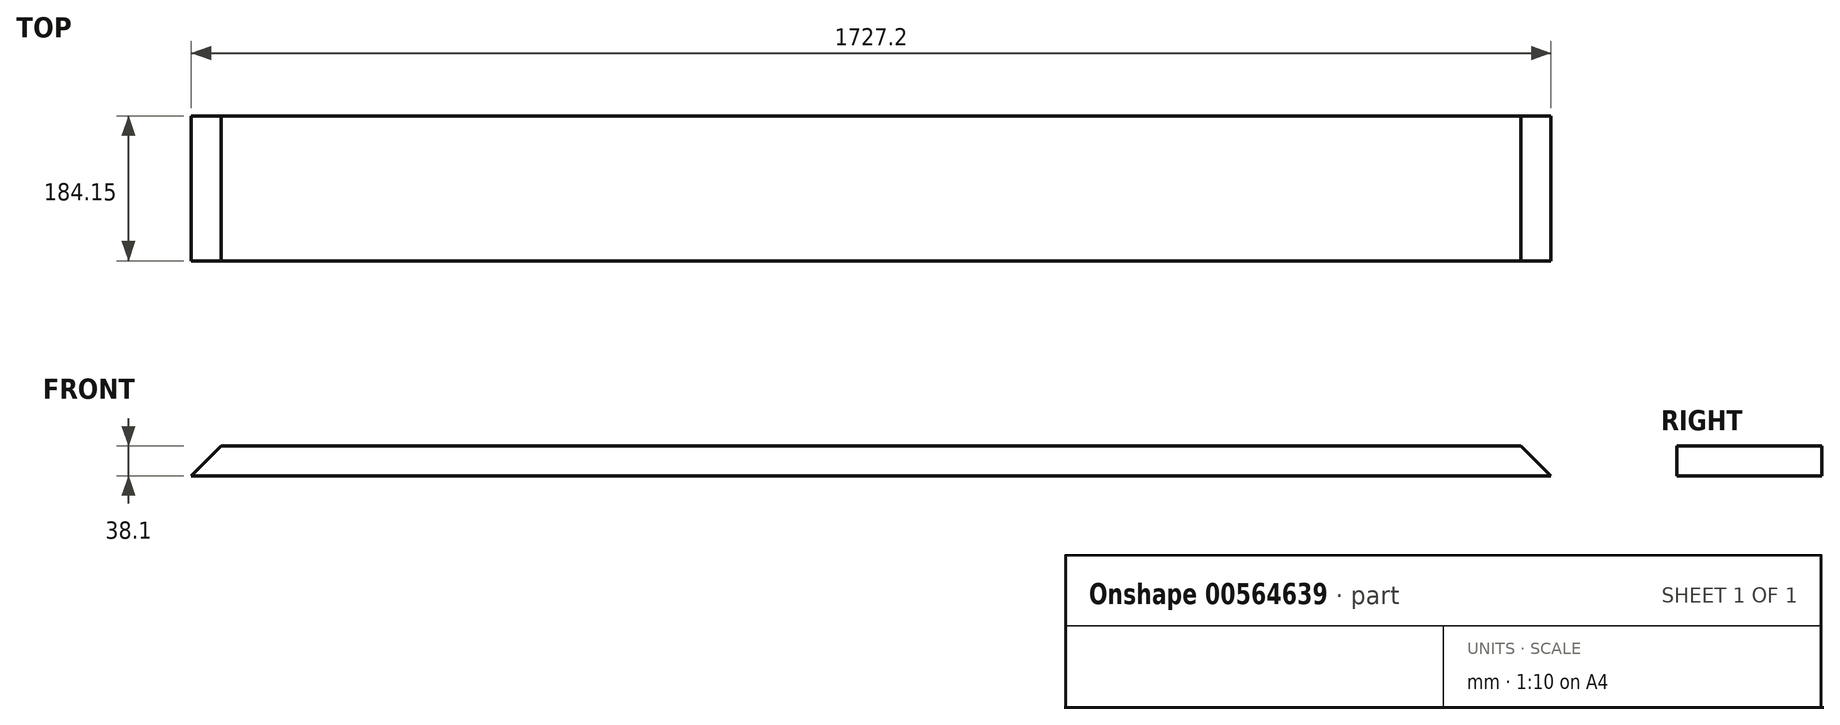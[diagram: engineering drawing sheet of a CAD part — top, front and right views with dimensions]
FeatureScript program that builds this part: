
annotation { "Feature Type Name" : "Feature", "Feature Type Description" : "" }
export const myFeature = defineFeature(function(context is Context, id is Id, definition is map)
    precondition{}
    {
        {
            var Q0;
            Q0=qCreatedBy(makeId("Top.planeOp"),FACE);
            var sketch = newSketch(context, id + "F0", { "sketchPlane" : qUnion([Q0])});
            skLineSegment(sketch, "E0.bottom", {"start": v(0, 0) * mm, "end": v(1727.2, 0) * mm});
            skLineSegment(sketch, "E0.top", {"start": v(0, 184.15) * mm, "end": v(1727.2, 184.15) * mm});
            skLineSegment(sketch, "E0.left", {"start": v(0, 0) * mm, "end": v(0, 184.15) * mm});
            skLineSegment(sketch, "E0.right", {"start": v(1727.2, 0) * mm, "end": v(1727.2, 184.15) * mm});
            skSolve(sketch);
        }
        {
            var Q0;
            Q0=makeQuery(id+"F0.imprint","IMPRINT",FACE,{"disambiguationData":[TD([[makeQuery(id+"F0.imprint","IMPRINT",EDGE,{"derivedFrom":sQuery(id+"F0.wireOp",EDGE,"E0.bottom")}),1.0]])]});
            extrude(context, id + "F1", {"entities" : qUnion([Q0]), "depth" : 38.1 * mm, "offsetDistance" : 25.4 * mm});
        }
        {
            var Q0;
            Q0=makeQuery(id+"F1.opExtrude","SWEPT_FACE",FACE,{"disambiguationData":[OSD([sQuery(id+"F0.wireOp",EDGE,"E0.bottom")])]});
            var sketch = newSketch(context, id + "F2", { "sketchPlane" : qUnion([Q0])});
            skLineSegment(sketch, "E1", {"start": v(0, 38.1) * mm, "end": v(0, 0) * mm});
            skLineSegment(sketch, "E2", {"start": v(0, 0) * mm, "end": v(38.1, 38.1) * mm});
            skLineSegment(sketch, "E3", {"start": v(38.1, 38.1) * mm, "end": v(0, 38.1) * mm});
            skLineSegment(sketch, "E4", {"start": v(1727.2, 0) * mm, "end": v(1727.2, 38.1) * mm});
            skLineSegment(sketch, "E5", {"start": v(1727.2, 38.1) * mm, "end": v(1689.1, 38.1) * mm});
            skLineSegment(sketch, "E6", {"start": v(1689.1, 38.1) * mm, "end": v(1727.2, 0) * mm});
            skSolve(sketch);
        }
        {
            var Q0;
            Q0 = qSketchRegion(id + "F2", true);
            extrude(context, id + "F3", {"entities" : qUnion([Q0]), "operationType" : NewBodyOperationType.REMOVE, "oppositeDirection" : true, "depth" : 254 * mm, "offsetDistance" : 25.4 * mm});
        }
    });
